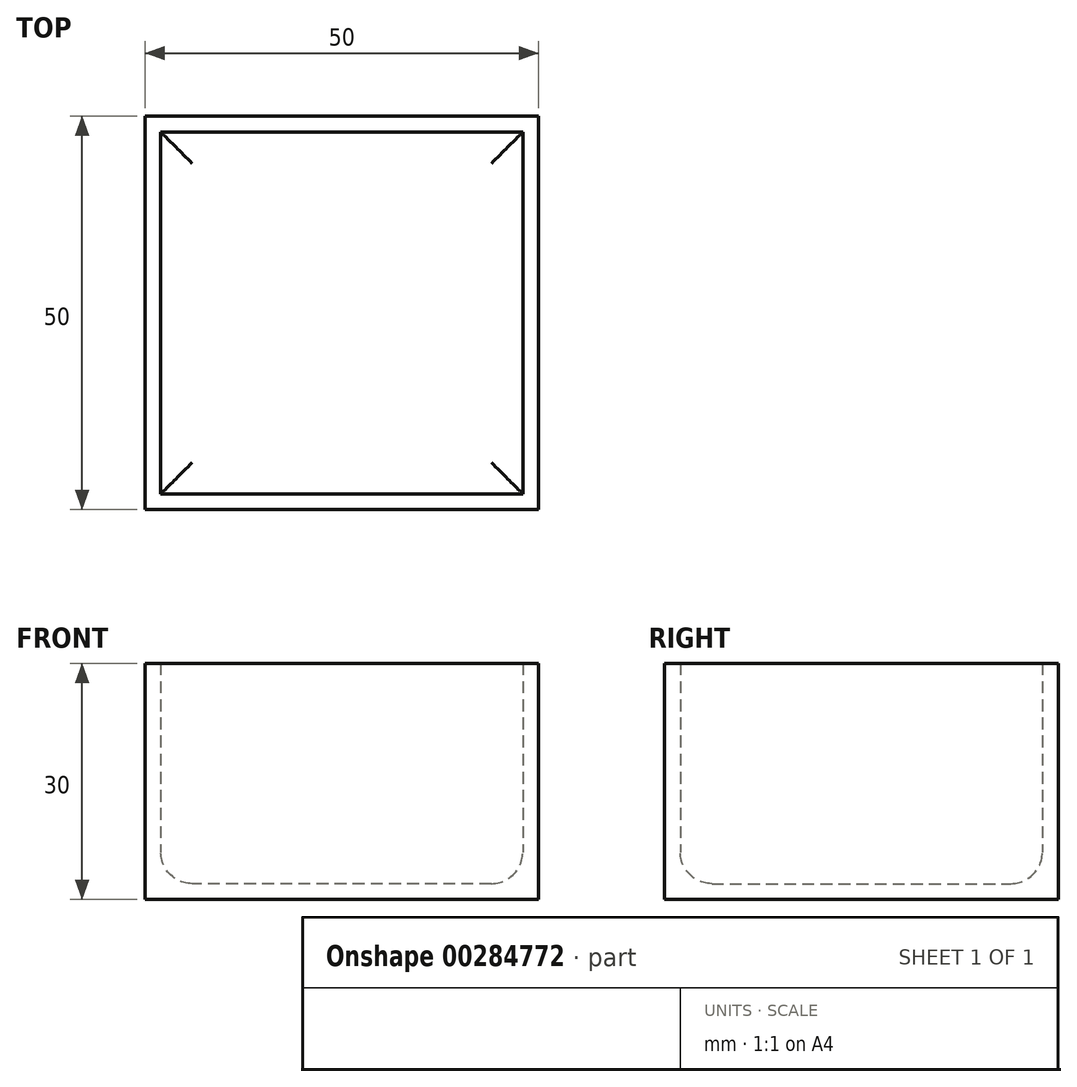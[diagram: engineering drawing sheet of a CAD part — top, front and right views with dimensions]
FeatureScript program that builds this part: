
annotation { "Feature Type Name" : "Feature", "Feature Type Description" : "" }
export const myFeature = defineFeature(function(context is Context, id is Id, definition is map)
    precondition{}
    {
        {
            assignVariable(context, id + "F0", {"name" : "hoehe", "anyValue" : 30});
        }
        {
            assignVariable(context, id + "F1", {"name" : "wand", "anyValue" : 2});
        }
        {
            var Q0;
            Q0=qCreatedBy(makeId("Top.planeOp"),FACE);
            var sketch = newSketch(context, id + "F2", { "sketchPlane" : qUnion([Q0])});
            skLineSegment(sketch, "E0.bottom", {"start": v(25, -25) * mm, "end": v(-25, -25) * mm});
            skLineSegment(sketch, "E0.top", {"start": v(25, 25) * mm, "end": v(-25, 25) * mm});
            skLineSegment(sketch, "E0.left", {"start": v(25, -25) * mm, "end": v(25, 25) * mm});
            skLineSegment(sketch, "E0.right", {"start": v(-25, -25) * mm, "end": v(-25, 25) * mm});
            skPoint(sketch, "E0.middle", {"position": v(0, 0) * mm});
            skSolve(sketch);
        }
        {
            var Q0;
            Q0 = qSketchRegion(id + "F2", true);
            extrude(context, id + "F3", {"entities" : qUnion([Q0]), "depth" : (getVariable(context, 'hoehe')) * mm});
        }
        {
            var Q0;
            Q0=makeQuery(id+"F3.opExtrude","CAP_FACE",FACE,{"disambiguationData":[OSD([sQuery(id+"F2.wireOp",EDGE,"E0.bottom"),sQuery(id+"F2.wireOp",EDGE,"E0.top"),sQuery(id+"F2.wireOp",EDGE,"E0.left"),sQuery(id+"F2.wireOp",EDGE,"E0.right")])],"isStart":false});
            var Q1;
            Q1=makeQuery(id+"F3.opExtrude","SWEPT_BODY",BODY,{"disambiguationData":[OSD([sQuery(id+"F2.wireOp",EDGE,"E0.bottom"),sQuery(id+"F2.wireOp",EDGE,"E0.top"),sQuery(id+"F2.wireOp",EDGE,"E0.left"),sQuery(id+"F2.wireOp",EDGE,"E0.right")])]});
            shell(context, id + "F4", {"entities" : qUnion([Q0]), "parts" : qUnion([Q1]), "thickness" : (getVariable(context, 'wand')) * mm});
        }
        {
            var Q0;
            {var subQ0=sQuery(id+"F2.wireOp",EDGE,"E0.top");Q0=makeQuery(id+"F4.opShell","OFFSET_EDGE",EDGE,{"disambiguationData":[OSD([subQ0]),TDD([makeQuery(id+"F3.opExtrude","CAP_EDGE",EDGE,{"disambiguationData":[OSD([subQ0])],"isStart":true})])]});}
            var Q1;
            {var subQ0=sQuery(id+"F2.wireOp",EDGE,"E0.right");Q1=makeQuery(id+"F4.opShell","OFFSET_EDGE",EDGE,{"disambiguationData":[OSD([subQ0]),TDD([makeQuery(id+"F3.opExtrude","CAP_EDGE",EDGE,{"disambiguationData":[OSD([subQ0])],"isStart":true})])]});}
            var Q2;
            {var subQ0=sQuery(id+"F2.wireOp",EDGE,"E0.left");Q2=makeQuery(id+"F4.opShell","OFFSET_EDGE",EDGE,{"disambiguationData":[OSD([subQ0]),TDD([makeQuery(id+"F3.opExtrude","CAP_EDGE",EDGE,{"disambiguationData":[OSD([subQ0])],"isStart":true})])]});}
            var Q3;
            {var subQ0=sQuery(id+"F2.wireOp",EDGE,"E0.bottom");Q3=makeQuery(id+"F4.opShell","OFFSET_EDGE",EDGE,{"disambiguationData":[OSD([subQ0]),TDD([makeQuery(id+"F3.opExtrude","CAP_EDGE",EDGE,{"disambiguationData":[OSD([subQ0])],"isStart":true})])]});}
            fillet(context, id + "F5", {"entities" : qUnion([Q0, Q1, Q2, Q3]), "radius" : 4 * mm, "allowEdgeOverflow" : false});
        }
    });
